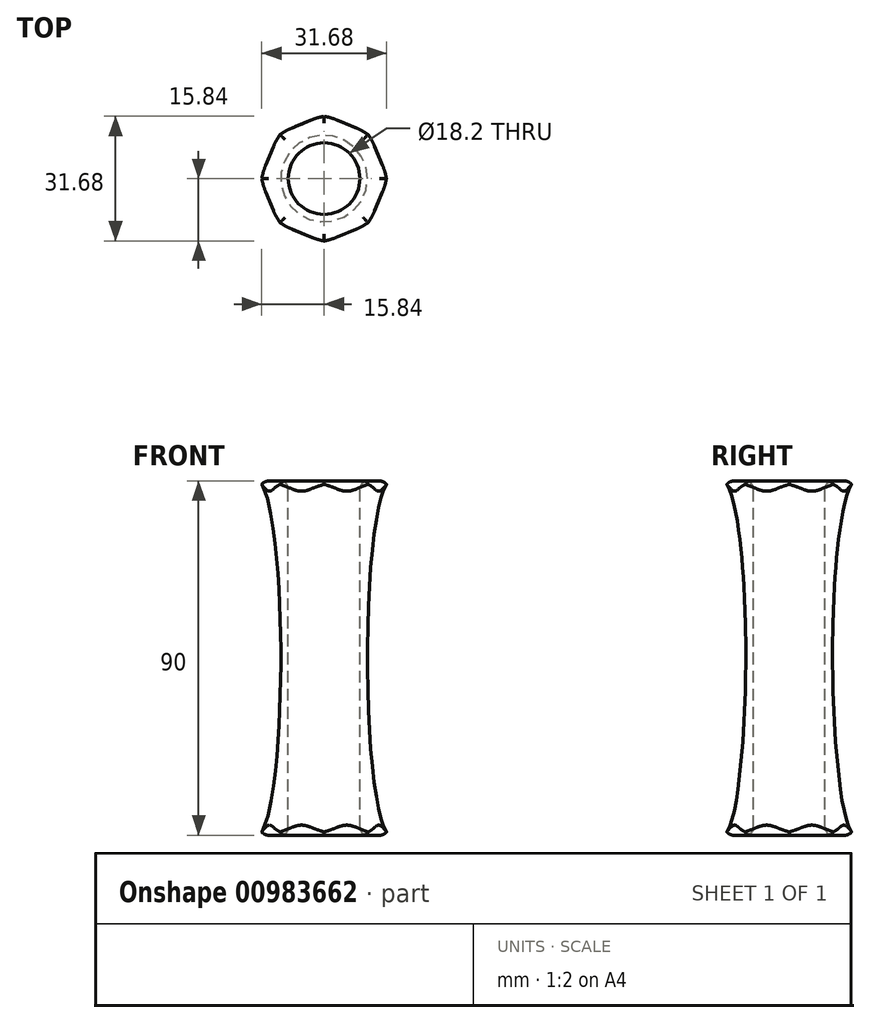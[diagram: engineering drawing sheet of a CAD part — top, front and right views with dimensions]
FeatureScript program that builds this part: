
annotation { "Feature Type Name" : "Feature", "Feature Type Description" : "" }
export const myFeature = defineFeature(function(context is Context, id is Id, definition is map)
    precondition{}
    {
        {
            var Q0;
            Q0=qCreatedBy(makeId("Top.planeOp"),FACE);
            var sketch = newSketch(context, id + "F0", { "sketchPlane" : qUnion([Q0])});
            skCircle(sketch, "E0", {"center": v(0, 0) * mm, "radius": 9.1 * mm});
            skCircle(sketch, "E1.cCircle", {"center": v(0, 0) * mm, "radius": 15 * mm, "construction": true});
            skLineSegment(sketch, "E1.0", {"start": v(11.48, 11.48) * mm, "end": v(16.24, 0) * mm});
            skLineSegment(sketch, "E1.1", {"start": v(16.24, 0) * mm, "end": v(11.48, -11.48) * mm});
            skLineSegment(sketch, "E1.2", {"start": v(11.48, -11.48) * mm, "end": v(0, -16.24) * mm});
            skLineSegment(sketch, "E1.3", {"start": v(0, -16.24) * mm, "end": v(-11.48, -11.48) * mm});
            skLineSegment(sketch, "E1.4", {"start": v(-11.48, -11.48) * mm, "end": v(-16.24, 0) * mm});
            skLineSegment(sketch, "E1.5", {"start": v(-16.24, 0) * mm, "end": v(-11.48, 11.48) * mm});
            skLineSegment(sketch, "E1.6", {"start": v(-11.48, 11.48) * mm, "end": v(0, 16.24) * mm});
            skLineSegment(sketch, "E1.7", {"start": v(0, 16.24) * mm, "end": v(11.48, 11.48) * mm});
            skPoint(sketch, "E1.0.midPoint", {"position": v(13.86, 5.74) * mm});
            skSolve(sketch);
        }
        {
            var Q0;
            Q0=makeQuery(id+"F0.imprint","IMPRINT",FACE,{"disambiguationData":[TD([[makeQuery(id+"F0.imprint","IMPRINT",EDGE,{"derivedFrom":sQuery(id+"F0.wireOp",EDGE,"E0")}),-1.0]])]});
            extrude(context, id + "F1", {"entities" : qUnion([Q0]), "oppositeDirection" : true, "depth" : 90 * mm, "offsetDistance" : 25 * mm});
        }
        {
            var Q0;
            Q0=qCreatedBy(makeId("Front.planeOp"),FACE);
            var sketch = newSketch(context, id + "F2", { "sketchPlane" : qUnion([Q0])});
            skLineSegment(sketch, "E2", {"start": v(0, 0) * mm, "end": v(15, 0) * mm, "construction": true});
            skLineSegment(sketch, "E3", {"start": v(15, 0) * mm, "end": v(15, -90) * mm, "construction": true});
            skEllipticalArc(sketch, "E4", {});
            skLineSegment(sketch, "E5", {"start": v(17, 0) * mm, "end": v(25, 0) * mm});
            skLineSegment(sketch, "E6", {"start": v(25, 0) * mm, "end": v(25, -90) * mm});
            skPoint(sketch, "E6.endSnap0", {"position": v(15, -86.1) * mm});
            skLineSegment(sketch, "E7", {"start": v(25, -90) * mm, "end": v(17, -90) * mm});
            skPoint(sketch, "E8", {"position": v(25, -45) * mm});
            skPoint(sketch, "E9", {"position": v(11, -45) * mm});
            const initialGuessF2  = {"E4": [0.017, -0.045, 0, 1, 0.045, 0.006, 0, 3.141592653589793]};
            skSetInitialGuess(sketch, initialGuessF2);
            skSolve(sketch);
        }
        {
            var Q0;
            Q0=qCreatedBy(makeId("Front.planeOp"),FACE);
            var sketch = newSketch(context, id + "F3", { "sketchPlane" : qUnion([Q0])});
            skLineSegment(sketch, "E10", {"start": v(0, 15.04) * mm, "end": v(0, -104.07) * mm, "construction": true});
            skSolve(sketch);
        }
        {
            var Q0;
            Q0 = qSketchRegion(id + "F2", true);
            var Q1;
            Q1=sQuery(id+"F3.wireOp",EDGE,"E10");
            revolve(context, id + "F4", {"operationType" : NewBodyOperationType.REMOVE, "surfaceOperationType" : NewSurfaceOperationType.NEW, "entities" : qUnion([Q0]), "axis" : qUnion([Q1]), "revolveType" : RevolveType.FULL, "oppositeDirection" : true});
        }
        {
            var Q0;
            Q0=makeQuery(id+"F1.opExtrude","CAP_FACE",FACE,{"disambiguationData":[OSD([sQuery(id+"F0.wireOp",EDGE,"E0"),sQuery(id+"F0.wireOp",EDGE,"E1.0"),sQuery(id+"F0.wireOp",EDGE,"E1.1"),sQuery(id+"F0.wireOp",EDGE,"E1.2"),sQuery(id+"F0.wireOp",EDGE,"E1.3"),sQuery(id+"F0.wireOp",EDGE,"E1.4"),sQuery(id+"F0.wireOp",EDGE,"E1.5"),sQuery(id+"F0.wireOp",EDGE,"E1.6"),sQuery(id+"F0.wireOp",EDGE,"E1.7")])],"isStart":true});
            var Q1;
            Q1=makeQuery(id+"F1.opExtrude","CAP_FACE",FACE,{"disambiguationData":[OSD([sQuery(id+"F0.wireOp",EDGE,"E0"),sQuery(id+"F0.wireOp",EDGE,"E1.0"),sQuery(id+"F0.wireOp",EDGE,"E1.1"),sQuery(id+"F0.wireOp",EDGE,"E1.2"),sQuery(id+"F0.wireOp",EDGE,"E1.3"),sQuery(id+"F0.wireOp",EDGE,"E1.4"),sQuery(id+"F0.wireOp",EDGE,"E1.5"),sQuery(id+"F0.wireOp",EDGE,"E1.6"),sQuery(id+"F0.wireOp",EDGE,"E1.7")])],"isStart":false});
            fillet(context, id + "F5", {"entities" : qUnion([Q0, Q1]), "radius" : 2 * mm, "tangentPropagation" : true, "allowEdgeOverflow" : false});
        }
    });
